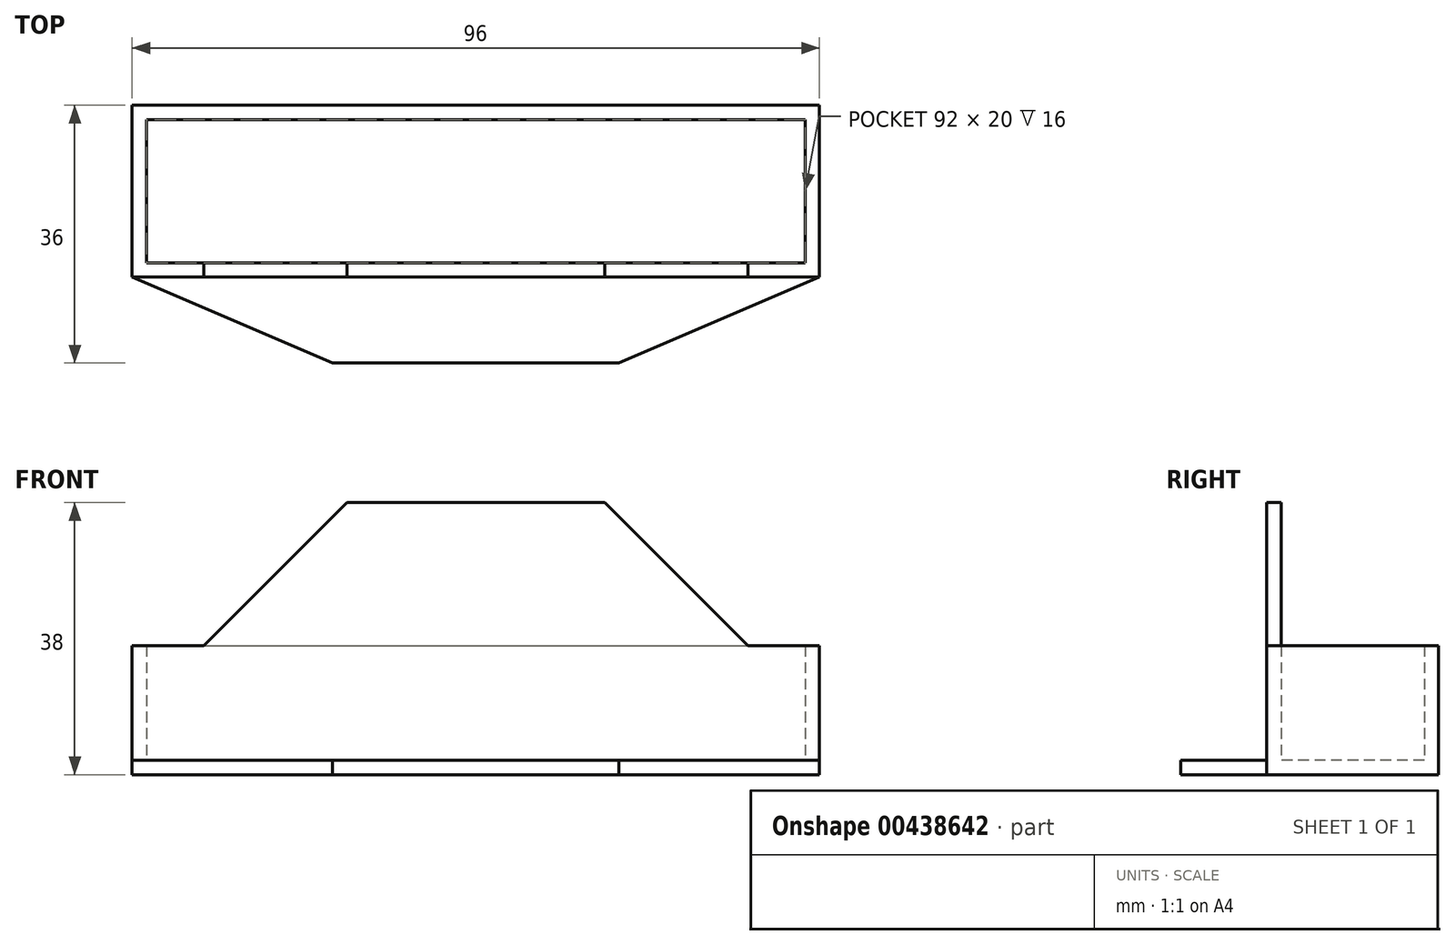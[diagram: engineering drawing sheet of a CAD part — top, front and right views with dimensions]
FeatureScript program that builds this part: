
annotation { "Feature Type Name" : "Feature", "Feature Type Description" : "" }
export const myFeature = defineFeature(function(context is Context, id is Id, definition is map)
    precondition{}
    {
        {
            var Q0;
            Q0=qCreatedBy(makeId("Top.planeOp"),FACE);
            var sketch = newSketch(context, id + "F0", { "sketchPlane" : qUnion([Q0])});
            skLineSegment(sketch, "E0.bottom", {"start": v(0, 0) * mm, "end": v(96, 0) * mm});
            skLineSegment(sketch, "E0.top", {"start": v(0, 24) * mm, "end": v(96, 24) * mm});
            skLineSegment(sketch, "E0.left", {"start": v(0, 0) * mm, "end": v(0, 24) * mm});
            skLineSegment(sketch, "E0.right", {"start": v(96, 0) * mm, "end": v(96, 24) * mm});
            skLineSegment(sketch, "E1", {"start": v(0, 0) * mm, "end": v(28, -12) * mm});
            skLineSegment(sketch, "E2", {"start": v(28, -12) * mm, "end": v(68, -12) * mm});
            skLineSegment(sketch, "E3", {"start": v(68, -12) * mm, "end": v(96, 0) * mm});
            skSolve(sketch);
        }
        {
            var Q0;
            Q0=makeQuery(id+"F0.imprint","IMPRINT",FACE,{"disambiguationData":[TD([[makeQuery(id+"F0.imprint","IMPRINT",EDGE,{"derivedFrom":sQuery(id+"F0.wireOp",EDGE,"E0.bottom")}),1.0]])]});
            extrude(context, id + "F1", {"entities" : qUnion([Q0]), "depth" : 2 * mm});
        }
        {
            var Q0;
            Q0=makeQuery(id+"F1.opExtrude","CAP_FACE",FACE,{"disambiguationData":[OSD([sQuery(id+"F0.wireOp",EDGE,"E0.bottom"),sQuery(id+"F0.wireOp",EDGE,"E0.top"),sQuery(id+"F0.wireOp",EDGE,"E0.left"),sQuery(id+"F0.wireOp",EDGE,"E0.right")])],"isStart":false});
            var sketch = newSketch(context, id + "F2", { "sketchPlane" : qUnion([Q0])});
            skLineSegment(sketch, "E4", {"start": v(2, 24) * mm, "end": v(2, 0) * mm});
            skLineSegment(sketch, "E5", {"start": v(2, 22) * mm, "end": v(96, 22) * mm});
            skLineSegment(sketch, "E6", {"start": v(94, 24) * mm, "end": v(94, 0) * mm});
            skLineSegment(sketch, "E7", {"start": v(0, 2) * mm, "end": v(96, 2) * mm});
            skLineSegment(sketch, "E8", {"start": v(30, 2) * mm, "end": v(30, 0) * mm});
            skLineSegment(sketch, "E9", {"start": v(66, 0) * mm, "end": v(66, 2) * mm});
            skSolve(sketch);
        }
        {
            var Q0;
            {var subQ0=sQuery(id+"F2.wireOp",EDGE,"E8");Q0=makeQuery(id+"F2.imprint","IMPRINT",FACE,{"disambiguationData":[TD([[makeQuery(id+"F2.imprint","IMPRINT",EDGE,{"derivedFrom":subQ0}),1.0]])]});}
            extrude(context, id + "F3", {"entities" : qUnion([Q0]), "operationType" : NewBodyOperationType.ADD, "depth" : 36 * mm, "offsetDistance" : 25 * mm});
        }
        {
            var Q0;
            {var subQ0=sQuery(id+"F2.wireOp",EDGE,"E4");var subQ1=makeQuery(id+"F1.opExtrude","CAP_EDGE",EDGE,{"disambiguationData":[OSD([sQuery(id+"F0.wireOp",EDGE,"E0.top")])],"isStart":false});var subQ2=makeQuery(id+"F2.imprint","INTERSECT",VERTEX,{"derivedFrom":[subQ1,subQ0]});Q0=makeQuery(id+"F2.imprint","IMPRINT",FACE,{"disambiguationData":[TD([[makeQuery(id+"F2.imprint","IMPRINT",EDGE,{"disambiguationData":[TD([[subQ2,-1.0]])],"derivedFrom":subQ0}),1.0]])]});}
            var Q1;
            {var subQ0=sQuery(id+"F2.wireOp",EDGE,"E5");var subQ1=makeQuery(id+"F1.opExtrude","CAP_EDGE",EDGE,{"disambiguationData":[OSD([sQuery(id+"F0.wireOp",EDGE,"E0.right")])],"isStart":false});var subQ2=makeQuery(id+"F2.imprint","INTERSECT",VERTEX,{"derivedFrom":[subQ1,subQ0]});Q1=makeQuery(id+"F2.imprint","IMPRINT",FACE,{"disambiguationData":[TD([[makeQuery(id+"F2.imprint","IMPRINT",EDGE,{"disambiguationData":[TD([[subQ2,1.0]])],"derivedFrom":subQ0}),1.0]])]});}
            var Q2;
            {var subQ5=sQuery(id+"F2.wireOp",EDGE,"E8");Q2=makeQuery(id+"F2.imprint","IMPRINT",FACE,{"disambiguationData":[TD([[makeQuery(id+"F2.imprint","IMPRINT",EDGE,{"derivedFrom":subQ5}),1.0]])]});}
            var Q3;
            {var subQ0=sQuery(id+"F2.wireOp",EDGE,"E5");var subQ1=makeQuery(id+"F1.opExtrude","CAP_EDGE",EDGE,{"disambiguationData":[OSD([sQuery(id+"F0.wireOp",EDGE,"E0.right")])],"isStart":false});var subQ2=makeQuery(id+"F2.imprint","INTERSECT",VERTEX,{"derivedFrom":[subQ1,subQ0]});Q3=makeQuery(id+"F2.imprint","IMPRINT",FACE,{"disambiguationData":[TD([[makeQuery(id+"F2.imprint","IMPRINT",EDGE,{"disambiguationData":[TD([[subQ2,1.0]])],"derivedFrom":subQ0}),-1.0]])]});}
            var Q4;
            {var subQ0=sQuery(id+"F2.wireOp",EDGE,"E6");var subQ1=makeQuery(id+"F1.opExtrude","CAP_EDGE",EDGE,{"disambiguationData":[OSD([sQuery(id+"F0.wireOp",EDGE,"E0.bottom")])],"isStart":false});var subQ2=makeQuery(id+"F2.imprint","INTERSECT",VERTEX,{"derivedFrom":[subQ1,subQ0]});Q4=makeQuery(id+"F2.imprint","IMPRINT",FACE,{"disambiguationData":[TD([[makeQuery(id+"F2.imprint","IMPRINT",EDGE,{"disambiguationData":[TD([[subQ2,1.0]])],"derivedFrom":subQ0}),1.0]])]});}
            var Q5;
            {var subQ3=sQuery(id+"F2.wireOp",EDGE,"E4");var subQ6=makeQuery(id+"F1.opExtrude","CAP_EDGE",EDGE,{"disambiguationData":[OSD([sQuery(id+"F0.wireOp",EDGE,"E0.top")])],"isStart":false});var subQ8=makeQuery(id+"F2.imprint","INTERSECT",VERTEX,{"derivedFrom":[subQ6,subQ3]});Q5=makeQuery(id+"F2.imprint","IMPRINT",FACE,{"disambiguationData":[TD([[makeQuery(id+"F2.imprint","IMPRINT",EDGE,{"disambiguationData":[TD([[subQ8,-1.0]])],"derivedFrom":subQ3}),-1.0]])]});}
            var Q6;
            {var subQ0=sQuery(id+"F2.wireOp",EDGE,"E4");var subQ1=makeQuery(id+"F1.opExtrude","CAP_EDGE",EDGE,{"disambiguationData":[OSD([sQuery(id+"F0.wireOp",EDGE,"E0.bottom")])],"isStart":false});var subQ2=makeQuery(id+"F2.imprint","INTERSECT",VERTEX,{"derivedFrom":[subQ1,subQ0]});Q6=makeQuery(id+"F2.imprint","IMPRINT",FACE,{"disambiguationData":[TD([[makeQuery(id+"F2.imprint","IMPRINT",EDGE,{"disambiguationData":[TD([[subQ2,1.0]])],"derivedFrom":subQ0}),-1.0]])]});}
            var Q7;
            {var subQ5=sQuery(id+"F2.wireOp",EDGE,"E8");Q7=makeQuery(id+"F2.imprint","IMPRINT",FACE,{"disambiguationData":[TD([[makeQuery(id+"F2.imprint","IMPRINT",EDGE,{"derivedFrom":subQ5}),-1.0]])]});}
            var Q8;
            {var subQ5=sQuery(id+"F2.wireOp",EDGE,"E9");Q8=makeQuery(id+"F2.imprint","IMPRINT",FACE,{"disambiguationData":[TD([[makeQuery(id+"F2.imprint","IMPRINT",EDGE,{"derivedFrom":subQ5}),-1.0]])]});}
            extrude(context, id + "F4", {"entities" : qUnion([Q0, Q1, Q2, Q3, Q4, Q5, Q6, Q7, Q8]), "operationType" : NewBodyOperationType.ADD, "depth" : 16 * mm, "offsetDistance" : 25 * mm});
        }
        {
            var Q0;
            Q0=makeQuery(id+"F4.opExtrude","CAP_EDGE",EDGE,{"disambiguationData":[OSD([sQuery(id+"F2.wireOp",EDGE,"E8")])],"isStart":false});
            var Q1;
            Q1=makeQuery(id+"F4.boolean.opBoolean","INTERSECT",EDGE,{"derivedFrom":[makeQuery(id+"F3.opExtrude","SWEPT_FACE",FACE,{"disambiguationData":[OSD([sQuery(id+"F2.wireOp",EDGE,"E8")])]}),makeQuery(id+"F4.opExtrude","CAP_FACE",FACE,{"disambiguationData":[OSD([sQuery(id+"F0.wireOp",EDGE,"E0.bottom"),sQuery(id+"F0.wireOp",EDGE,"E0.top"),sQuery(id+"F0.wireOp",EDGE,"E0.left"),sQuery(id+"F0.wireOp",EDGE,"E0.right"),sQuery(id+"F2.wireOp",EDGE,"E4"),sQuery(id+"F2.wireOp",EDGE,"E5"),sQuery(id+"F2.wireOp",EDGE,"E6"),sQuery(id+"F2.wireOp",EDGE,"E7")])],"isStart":false})]});
            var Q2;
            Q2=makeQuery(id+"F4.boolean.opBoolean","INTERSECT",EDGE,{"derivedFrom":[makeQuery(id+"F3.opExtrude","SWEPT_FACE",FACE,{"disambiguationData":[OSD([sQuery(id+"F2.wireOp",EDGE,"E9")])]}),makeQuery(id+"F4.opExtrude","CAP_FACE",FACE,{"disambiguationData":[OSD([sQuery(id+"F0.wireOp",EDGE,"E0.bottom"),sQuery(id+"F0.wireOp",EDGE,"E0.top"),sQuery(id+"F0.wireOp",EDGE,"E0.left"),sQuery(id+"F0.wireOp",EDGE,"E0.right"),sQuery(id+"F2.wireOp",EDGE,"E4"),sQuery(id+"F2.wireOp",EDGE,"E5"),sQuery(id+"F2.wireOp",EDGE,"E6"),sQuery(id+"F2.wireOp",EDGE,"E7")])],"isStart":false})]});
            chamfer(context, id + "F5", {"entities" : qUnion([Q0, Q1, Q2]), "width" : 20 * mm, "tangentPropagation" : true});
        }
        {
            var Q0;
            Q0=makeQuery(id+"F0.imprint","IMPRINT",FACE,{"disambiguationData":[TD([[makeQuery(id+"F0.imprint","IMPRINT",EDGE,{"derivedFrom":sQuery(id+"F0.wireOp",EDGE,"E0.bottom")}),-1.0]])]});
            var Q1;
            Q1=makeQuery(id+"F1.opExtrude","CAP_FACE",FACE,{"disambiguationData":[OSD([sQuery(id+"F0.wireOp",EDGE,"E0.bottom"),sQuery(id+"F0.wireOp",EDGE,"E0.top"),sQuery(id+"F0.wireOp",EDGE,"E0.left"),sQuery(id+"F0.wireOp",EDGE,"E0.right")])],"isStart":false});
            extrude(context, id + "F6", {"entities" : qUnion([Q0]), "operationType" : NewBodyOperationType.ADD, "endBound" : BoundingType.UP_TO_SURFACE, "depth" : 25 * mm, "endBoundEntityFace" : qUnion([Q1]), "offsetDistance" : 25 * mm});
        }
    });
